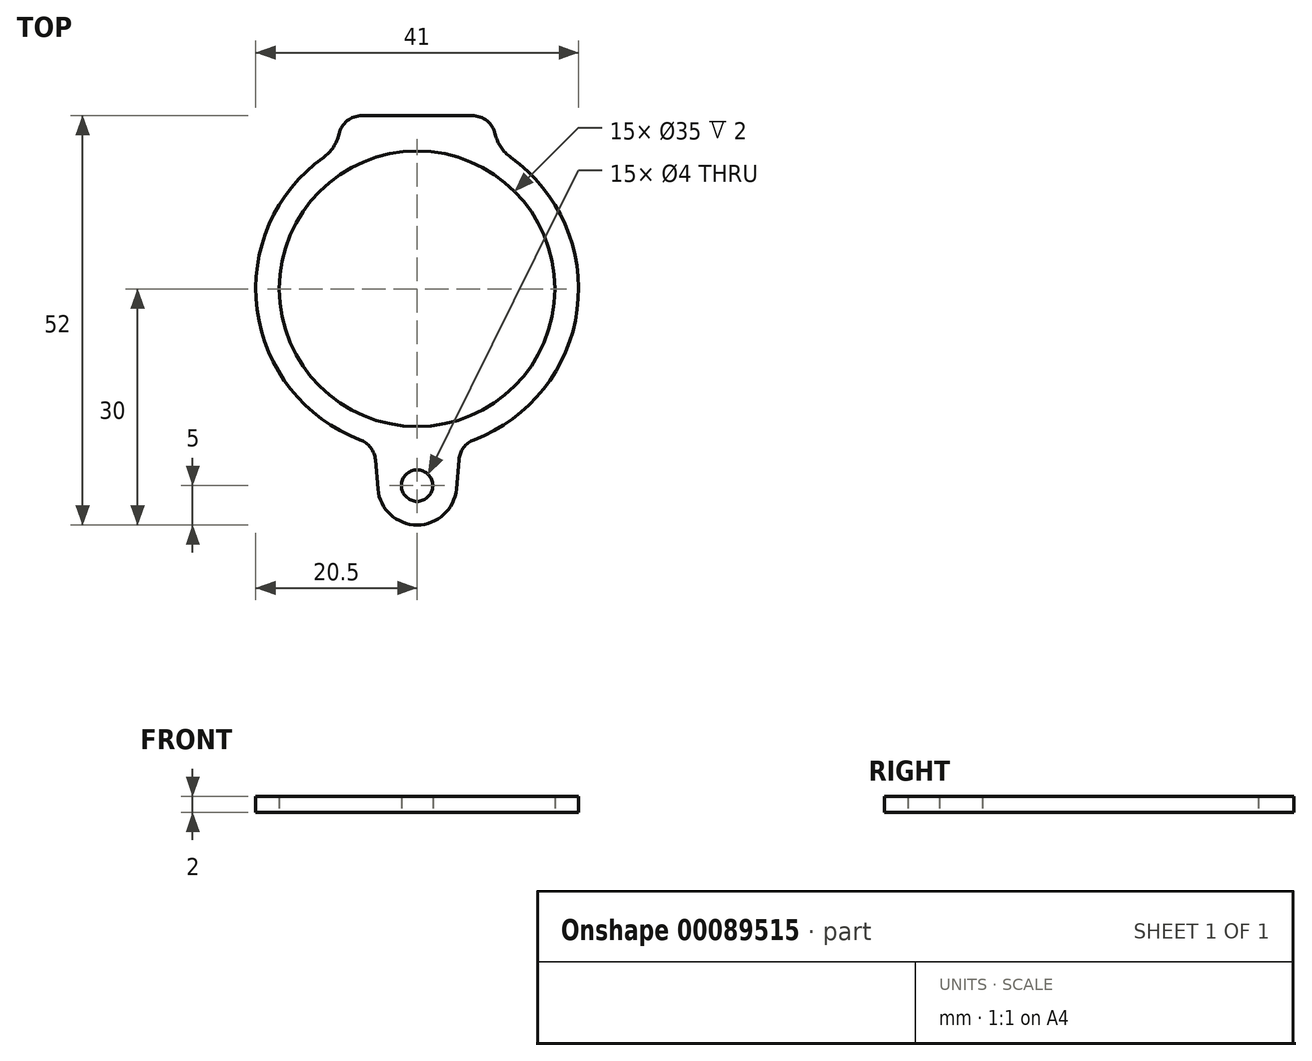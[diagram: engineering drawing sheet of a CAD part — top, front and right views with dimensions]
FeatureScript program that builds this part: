
annotation { "Feature Type Name" : "Feature", "Feature Type Description" : "" }
export const myFeature = defineFeature(function(context is Context, id is Id, definition is map)
    precondition{}
    {
        {
            var Q0;
            Q0=qCreatedBy(makeId("Top.planeOp"),FACE);
            var sketch = newSketch(context, id + "F0", { "sketchPlane" : qUnion([Q0])});
            skArc(sketch, "E0", {"start": v(-10, 17.9) * mm, "mid": v(-20.35, -2.44) * mm, "end": v(-5.48, -19.75) * mm});
            skCircle(sketch, "E1", {"center": v(0, 0) * mm, "radius": 17.5 * mm});
            skLineSegment(sketch, "E2", {"start": v(0, 53.3) * mm, "end": v(0, -55.37) * mm, "construction": true});
            skLineSegment(sketch, "E3.bottom", {"start": v(-10, 22) * mm, "end": v(10, 22) * mm});
            skLineSegment(sketch, "E3.left", {"start": v(-10, 22) * mm, "end": v(-10, 17.9) * mm});
            skLineSegment(sketch, "E3.right", {"start": v(10, 22) * mm, "end": v(10, 17.9) * mm});
            skArc(sketch, "E4", {"start": v(-4.98, -25.44) * mm, "mid": v(0, -30) * mm, "end": v(4.98, -25.44) * mm});
            skArc(sketch, "E5.trimOffspring", {"start": v(5.48, -19.75) * mm, "mid": v(20.35, -2.44) * mm, "end": v(10, 17.9) * mm});
            skCircle(sketch, "E6", {"center": v(0, -25) * mm, "radius": 2 * mm});
            skLineSegment(sketch, "E7", {"start": v(-5.48, -19.75) * mm, "end": v(-4.98, -25.44) * mm});
            skLineSegment(sketch, "E8", {"start": v(5.48, -19.75) * mm, "end": v(4.98, -25.44) * mm});
            skSolve(sketch);
        }
        {
            var Q0;
            Q0 = qSketchRegion(id + "F0", true);
            extrude(context, id + "F1", {"entities" : qUnion([Q0]), "depth" : 2 * mm});
        }
        {
            var Q0;
            Q0=makeQuery(id+"F1.opExtrude","SWEPT_EDGE",EDGE,{"disambiguationData":[OSD([sQuery(id+"F0.wireOp",EDGE,"E3.bottom"),sQuery(id+"F0.wireOp",EDGE,"E3.left")])]});
            var Q1;
            Q1=makeQuery(id+"F1.opExtrude","SWEPT_EDGE",EDGE,{"disambiguationData":[OSD([sQuery(id+"F0.wireOp",EDGE,"E3.bottom"),sQuery(id+"F0.wireOp",EDGE,"E3.right")])]});
            var Q2;
            Q2=makeQuery(id+"F1.opExtrude","SWEPT_EDGE",EDGE,{"disambiguationData":[OSD([sQuery(id+"F0.wireOp",EDGE,"E0"),sQuery(id+"F0.wireOp",EDGE,"E7")])]});
            var Q3;
            Q3=makeQuery(id+"F1.opExtrude","SWEPT_EDGE",EDGE,{"disambiguationData":[OSD([sQuery(id+"F0.wireOp",EDGE,"E5.trimOffspring"),sQuery(id+"F0.wireOp",EDGE,"E8")])]});
            fillet(context, id + "F2", {"entities" : qUnion([Q0, Q1, Q2, Q3]), "radius" : 3 * mm, "tangentPropagation" : true, "allowEdgeOverflow" : false});
        }
        {
            var Q0;
            Q0=makeQuery(id+"F1.opExtrude","SWEPT_EDGE",EDGE,{"disambiguationData":[OSD([sQuery(id+"F0.wireOp",EDGE,"E0"),sQuery(id+"F0.wireOp",EDGE,"E3.left")])]});
            var Q1;
            Q1=makeQuery(id+"F1.opExtrude","SWEPT_EDGE",EDGE,{"disambiguationData":[OSD([sQuery(id+"F0.wireOp",EDGE,"E3.right"),sQuery(id+"F0.wireOp",EDGE,"E5.trimOffspring")])]});
            fillet(context, id + "F3", {"entities" : qUnion([Q0, Q1]), "radius" : 5 * mm, "tangentPropagation" : true, "allowEdgeOverflow" : false});
        }
    });
